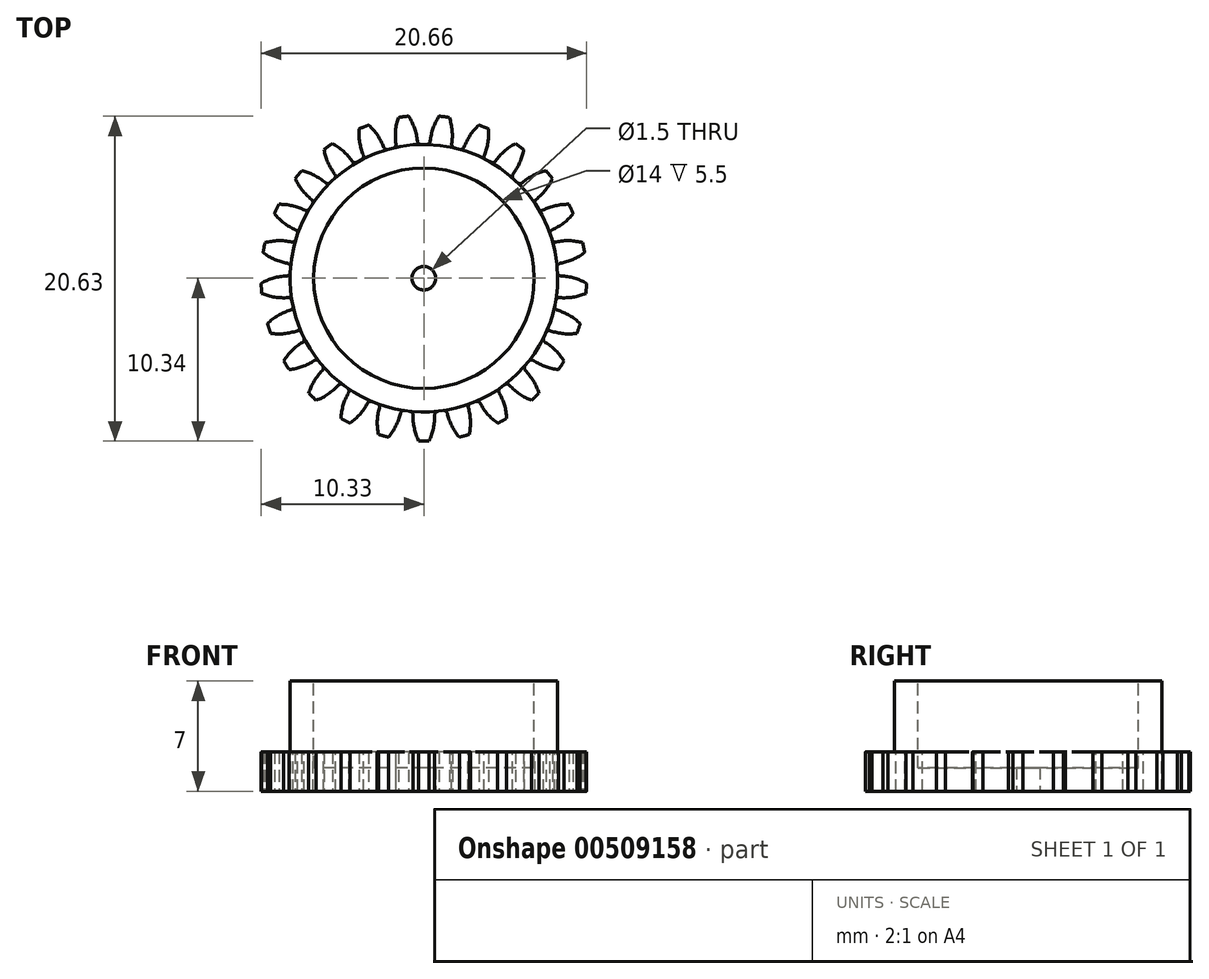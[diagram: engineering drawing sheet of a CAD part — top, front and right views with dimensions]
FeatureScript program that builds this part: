
annotation { "Feature Type Name" : "Feature", "Feature Type Description" : "" }
export const myFeature = defineFeature(function(context is Context, id is Id, definition is map)
    precondition{}
    {
        {
            assignVariable(context, id + "F0", {"name" : "mod", "anyValue" : 17 / 22.2});
        }
        {
            var Q0;
            Q0=qCreatedBy(makeId("Top.planeOp"),FACE);
            var sketch = newSketch(context, id + "F1", { "sketchPlane" : qUnion([Q0])});
            skCircle(sketch, "E0", {"center": v(0, 0) * mm, "radius": 7 * mm});
            skCircle(sketch, "E1", {"center": v(0, 0) * mm, "radius": 8.5 * mm});
            skCircle(sketch, "E2", {"center": v(0, 0) * mm, "radius": 9.57 * mm});
            skCircle(sketch, "E3", {"center": v(0, 0) * mm, "radius": 10.34 * mm});
            skCircle(sketch, "E4", {"center": v(0, 0) * mm, "radius": 0.75 * mm});
            skSolve(sketch);
        }
        {
            var Q0;
            Q0=makeQuery(id+"F1.imprint","IMPRINT",FACE,{"disambiguationData":[TD([[makeQuery(id+"F1.imprint","IMPRINT",EDGE,{"derivedFrom":sQuery(id+"F1.wireOp",EDGE,"E0")}),1.0]])]});
            var Q1;
            Q1=makeQuery(id+"F1.imprint","IMPRINT",FACE,{"disambiguationData":[TD([[makeQuery(id+"F1.imprint","IMPRINT",EDGE,{"derivedFrom":sQuery(id+"F1.wireOp",EDGE,"E0")}),-1.0]])]});
            var Q2;
            Q2=makeQuery(id+"F1.imprint","IMPRINT",FACE,{"disambiguationData":[TD([[makeQuery(id+"F1.imprint","IMPRINT",EDGE,{"derivedFrom":sQuery(id+"F1.wireOp",EDGE,"E1")}),-1.0]])]});
            var Q3;
            Q3=makeQuery(id+"F1.imprint","IMPRINT",FACE,{"disambiguationData":[TD([[makeQuery(id+"F1.imprint","IMPRINT",EDGE,{"derivedFrom":sQuery(id+"F1.wireOp",EDGE,"E2")}),-1.0]])]});
            extrude(context, id + "F2", {"entities" : qUnion([Q0, Q1, Q2, Q3]), "depth" : 2.5 * mm});
        }
        {
            var Q0;
            Q0=qCreatedBy(makeId("Top.planeOp"),FACE);
            var sketch = newSketch(context, id + "F3", { "sketchPlane" : qUnion([Q0])});
            skLineSegment(sketch, "E5", {"start": v(0, 0) * mm, "end": v(0, 10.34) * mm, "construction": true});
            skArc(sketch, "E6", {"start": v(-0.39, 8.5) * mm, "mid": v(-0.8, 10) * mm, "end": v(-1.81, 11.2) * mm});
            skArc(sketch, "E7.MirrorCS", {"start": v(0.39, 8.5) * mm, "mid": v(0.8, 10) * mm, "end": v(1.81, 11.2) * mm});
            skArc(sketch, "E8.0", {"start": v(1.81, 11.2) * mm, "mid": v(0, 11.34) * mm, "end": v(-1.81, 11.2) * mm});
            skLineSegment(sketch, "E9", {"start": v(-0.6, 9.55) * mm, "end": v(0.6, 9.55) * mm, "construction": true});
            skArc(sketch, "E10.0", {"start": v(0.39, 8.5) * mm, "mid": v(0, 8.5) * mm, "end": v(-0.39, 8.5) * mm});
            skLineSegment(sketch, "E11", {"start": v(0, 0) * mm, "end": v(-0.39, 8.5) * mm, "construction": true});
            skLineSegment(sketch, "E12", {"start": v(0, 7.9) * mm, "end": v(-0.87, 10.3) * mm, "construction": true});
            skLineSegment(sketch, "E13", {"start": v(0, 0) * mm, "end": v(1.3, 10.26) * mm, "construction": true});
            skLineSegment(sketch, "E14", {"start": v(0.6, 9.55) * mm, "end": v(1.8, 9.4) * mm, "construction": true});
            skSolve(sketch);
        }
        {
            var Q0;
            Q0=makeQuery(id+"F3.imprint","IMPRINT",FACE,{"disambiguationData":[TD([[makeQuery(id+"F3.imprint","IMPRINT",EDGE,{"derivedFrom":sQuery(id+"F3.wireOp",EDGE,"E6")}),-1.0]])]});
            extrude(context, id + "F4", {"entities" : qUnion([Q0]), "operationType" : NewBodyOperationType.REMOVE, "endBound" : BoundingType.THROUGH_ALL, "depth" : 25 * mm});
        }
        {
            var Q0;
            Q0=makeQuery(id+"F4.boolean.opBoolean","COPY",EDGE,{"derivedFrom":makeQuery(id+"F4.opExtrude","SWEPT_EDGE",EDGE,{"disambiguationData":[OSD([sQuery(id+"F3.wireOp",EDGE,"E6"),sQuery(id+"F3.wireOp",EDGE,"E10.0")])]})});
            var Q1;
            Q1=makeQuery(id+"F4.boolean.opBoolean","COPY",EDGE,{"derivedFrom":makeQuery(id+"F4.opExtrude","SWEPT_EDGE",EDGE,{"disambiguationData":[OSD([sQuery(id+"F3.wireOp",EDGE,"E7.MirrorCS"),sQuery(id+"F3.wireOp",EDGE,"E10.0")])]})});
            fillet(context, id + "F5", {"entities" : qUnion([Q0, Q1]), "radius" : (.3 * getVariable(context, 'mod')) * mm, "tangentPropagation" : true, "allowEdgeOverflow" : false});
        }
        {
            var Q0;
            Q0=qCreatedBy(makeId("Front.planeOp"),FACE);
            var sketch = newSketch(context, id + "F6", { "sketchPlane" : qUnion([Q0])});
            skLineSegment(sketch, "E15", {"start": v(0, -1.68) * mm, "end": v(0, 5.16) * mm, "construction": true});
            skSolve(sketch);
        }
        {
            var Q0;
            Q0=makeQuery(id+"F2.opExtrude","SWEPT_BODY",BODY,{"disambiguationData":[OSD([sQuery(id+"F1.wireOp",EDGE,"E3")])]});
            var Q1;
            Q1=sQuery(id+"F6.wireOp",EDGE,"E15");
            circularPattern(context, id + "F7", {"entities" : qUnion([Q0]), "axis" : qUnion([Q1]), "angle" : 360 * degree, "instanceCount" : 25, "equalSpace" : true});
        }
        {
            var Q0;
            Q0=makeQuery(id+"F2.opExtrude","SWEPT_BODY",BODY,{"disambiguationData":[OSD([sQuery(id+"F1.wireOp",EDGE,"E3")])]});
            var Q1;
            Q1=makeQuery(id+"F7.opPattern","COPY",BODY,{"derivedFrom":makeQuery(id+"F2.opExtrude","SWEPT_BODY",BODY,{"disambiguationData":[OSD([sQuery(id+"F1.wireOp",EDGE,"E3")])]}),"instanceName":"1"});
            var Q2;
            Q2=makeQuery(id+"F7.opPattern","COPY",BODY,{"derivedFrom":makeQuery(id+"F2.opExtrude","SWEPT_BODY",BODY,{"disambiguationData":[OSD([sQuery(id+"F1.wireOp",EDGE,"E3")])]}),"instanceName":"2"});
            var Q3;
            Q3=makeQuery(id+"F7.opPattern","COPY",BODY,{"derivedFrom":makeQuery(id+"F2.opExtrude","SWEPT_BODY",BODY,{"disambiguationData":[OSD([sQuery(id+"F1.wireOp",EDGE,"E3")])]}),"instanceName":"3"});
            var Q4;
            Q4=makeQuery(id+"F7.opPattern","COPY",BODY,{"derivedFrom":makeQuery(id+"F2.opExtrude","SWEPT_BODY",BODY,{"disambiguationData":[OSD([sQuery(id+"F1.wireOp",EDGE,"E3")])]}),"instanceName":"4"});
            var Q5;
            Q5=makeQuery(id+"F7.opPattern","COPY",BODY,{"derivedFrom":makeQuery(id+"F2.opExtrude","SWEPT_BODY",BODY,{"disambiguationData":[OSD([sQuery(id+"F1.wireOp",EDGE,"E3")])]}),"instanceName":"5"});
            var Q6;
            Q6=makeQuery(id+"F7.opPattern","COPY",BODY,{"derivedFrom":makeQuery(id+"F2.opExtrude","SWEPT_BODY",BODY,{"disambiguationData":[OSD([sQuery(id+"F1.wireOp",EDGE,"E3")])]}),"instanceName":"6"});
            var Q7;
            Q7=makeQuery(id+"F7.opPattern","COPY",BODY,{"derivedFrom":makeQuery(id+"F2.opExtrude","SWEPT_BODY",BODY,{"disambiguationData":[OSD([sQuery(id+"F1.wireOp",EDGE,"E3")])]}),"instanceName":"7"});
            var Q8;
            Q8=makeQuery(id+"F7.opPattern","COPY",BODY,{"derivedFrom":makeQuery(id+"F2.opExtrude","SWEPT_BODY",BODY,{"disambiguationData":[OSD([sQuery(id+"F1.wireOp",EDGE,"E3")])]}),"instanceName":"8"});
            var Q9;
            Q9=makeQuery(id+"F7.opPattern","COPY",BODY,{"derivedFrom":makeQuery(id+"F2.opExtrude","SWEPT_BODY",BODY,{"disambiguationData":[OSD([sQuery(id+"F1.wireOp",EDGE,"E3")])]}),"instanceName":"10"});
            var Q10;
            Q10=makeQuery(id+"F7.opPattern","COPY",BODY,{"derivedFrom":makeQuery(id+"F2.opExtrude","SWEPT_BODY",BODY,{"disambiguationData":[OSD([sQuery(id+"F1.wireOp",EDGE,"E3")])]}),"instanceName":"11"});
            var Q11;
            Q11=makeQuery(id+"F7.opPattern","COPY",BODY,{"derivedFrom":makeQuery(id+"F2.opExtrude","SWEPT_BODY",BODY,{"disambiguationData":[OSD([sQuery(id+"F1.wireOp",EDGE,"E3")])]}),"instanceName":"12"});
            var Q12;
            Q12=makeQuery(id+"F7.opPattern","COPY",BODY,{"derivedFrom":makeQuery(id+"F2.opExtrude","SWEPT_BODY",BODY,{"disambiguationData":[OSD([sQuery(id+"F1.wireOp",EDGE,"E3")])]}),"instanceName":"13"});
            var Q13;
            Q13=makeQuery(id+"F7.opPattern","COPY",BODY,{"derivedFrom":makeQuery(id+"F2.opExtrude","SWEPT_BODY",BODY,{"disambiguationData":[OSD([sQuery(id+"F1.wireOp",EDGE,"E3")])]}),"instanceName":"14"});
            var Q14;
            Q14=makeQuery(id+"F7.opPattern","COPY",BODY,{"derivedFrom":makeQuery(id+"F2.opExtrude","SWEPT_BODY",BODY,{"disambiguationData":[OSD([sQuery(id+"F1.wireOp",EDGE,"E3")])]}),"instanceName":"15"});
            var Q15;
            Q15=makeQuery(id+"F7.opPattern","COPY",BODY,{"derivedFrom":makeQuery(id+"F2.opExtrude","SWEPT_BODY",BODY,{"disambiguationData":[OSD([sQuery(id+"F1.wireOp",EDGE,"E3")])]}),"instanceName":"16"});
            var Q16;
            Q16=makeQuery(id+"F7.opPattern","COPY",BODY,{"derivedFrom":makeQuery(id+"F2.opExtrude","SWEPT_BODY",BODY,{"disambiguationData":[OSD([sQuery(id+"F1.wireOp",EDGE,"E3")])]}),"instanceName":"17"});
            var Q17;
            Q17=makeQuery(id+"F7.opPattern","COPY",BODY,{"derivedFrom":makeQuery(id+"F2.opExtrude","SWEPT_BODY",BODY,{"disambiguationData":[OSD([sQuery(id+"F1.wireOp",EDGE,"E3")])]}),"instanceName":"18"});
            var Q18;
            Q18=makeQuery(id+"F7.opPattern","COPY",BODY,{"derivedFrom":makeQuery(id+"F2.opExtrude","SWEPT_BODY",BODY,{"disambiguationData":[OSD([sQuery(id+"F1.wireOp",EDGE,"E3")])]}),"instanceName":"19"});
            var Q19;
            Q19=makeQuery(id+"F7.opPattern","COPY",BODY,{"derivedFrom":makeQuery(id+"F2.opExtrude","SWEPT_BODY",BODY,{"disambiguationData":[OSD([sQuery(id+"F1.wireOp",EDGE,"E3")])]}),"instanceName":"20"});
            var Q20;
            Q20=makeQuery(id+"F7.opPattern","COPY",BODY,{"derivedFrom":makeQuery(id+"F2.opExtrude","SWEPT_BODY",BODY,{"disambiguationData":[OSD([sQuery(id+"F1.wireOp",EDGE,"E3")])]}),"instanceName":"21"});
            var Q21;
            Q21=makeQuery(id+"F7.opPattern","COPY",BODY,{"derivedFrom":makeQuery(id+"F2.opExtrude","SWEPT_BODY",BODY,{"disambiguationData":[OSD([sQuery(id+"F1.wireOp",EDGE,"E3")])]}),"instanceName":"24"});
            var Q22;
            Q22=makeQuery(id+"F7.opPattern","COPY",BODY,{"derivedFrom":makeQuery(id+"F2.opExtrude","SWEPT_BODY",BODY,{"disambiguationData":[OSD([sQuery(id+"F1.wireOp",EDGE,"E3")])]}),"instanceName":"23"});
            var Q23;
            Q23=makeQuery(id+"F7.opPattern","COPY",BODY,{"derivedFrom":makeQuery(id+"F2.opExtrude","SWEPT_BODY",BODY,{"disambiguationData":[OSD([sQuery(id+"F1.wireOp",EDGE,"E3")])]}),"instanceName":"22"});
            var Q24;
            Q24=makeQuery(id+"F7.opPattern","COPY",BODY,{"derivedFrom":makeQuery(id+"F2.opExtrude","SWEPT_BODY",BODY,{"disambiguationData":[OSD([sQuery(id+"F1.wireOp",EDGE,"E3")])]}),"instanceName":"9"});
            booleanBodies(context, id + "F8", {"operationType" : BooleanOperationType.INTERSECTION, "tools" : qUnion([Q0, Q1, Q2, Q3, Q4, Q5, Q6, Q7, Q8, Q9, Q10, Q11, Q12, Q13, Q14, Q15, Q16, Q17, Q18, Q19, Q20, Q21, Q22, Q23, Q24])});
        }
        {
            var Q0;
            Q0=makeQuery(id+"F1.imprint","IMPRINT",FACE,{"disambiguationData":[TD([[makeQuery(id+"F1.imprint","IMPRINT",EDGE,{"derivedFrom":sQuery(id+"F1.wireOp",EDGE,"E0")}),-1.0]])]});
            var Q1;
            Q1=makeQuery(id+"F1.imprint","IMPRINT",FACE,{"disambiguationData":[TD([[makeQuery(id+"F1.imprint","IMPRINT",EDGE,{"derivedFrom":sQuery(id+"F1.wireOp",EDGE,"E0")}),1.0]])]});
            extrude(context, id + "F9", {"entities" : qUnion([Q0, Q1]), "operationType" : NewBodyOperationType.ADD, "depth" : 7 * mm});
        }
        {
            var Q0;
            Q0=makeQuery(id+"F9.opExtrude","CAP_FACE",FACE,{"disambiguationData":[OSD([sQuery(id+"F1.wireOp",EDGE,"E1")])],"isStart":false});
            var sketch = newSketch(context, id + "F10", { "sketchPlane" : qUnion([Q0])});
            skCircle(sketch, "E16.0", {"center": v(0, 0) * mm, "radius": 7 * mm});
            skSolve(sketch);
        }
        {
            var Q0;
            Q0=makeQuery(id+"F10.imprint","IMPRINT",FACE,{"disambiguationData":[TD([[makeQuery(id+"F10.imprint","IMPRINT",EDGE,{"derivedFrom":sQuery(id+"F10.wireOp",EDGE,"E16.0")}),1.0]])]});
            extrude(context, id + "F11", {"entities" : qUnion([Q0]), "operationType" : NewBodyOperationType.REMOVE, "oppositeDirection" : true, "depth" : 5.5 * mm});
        }
    });
